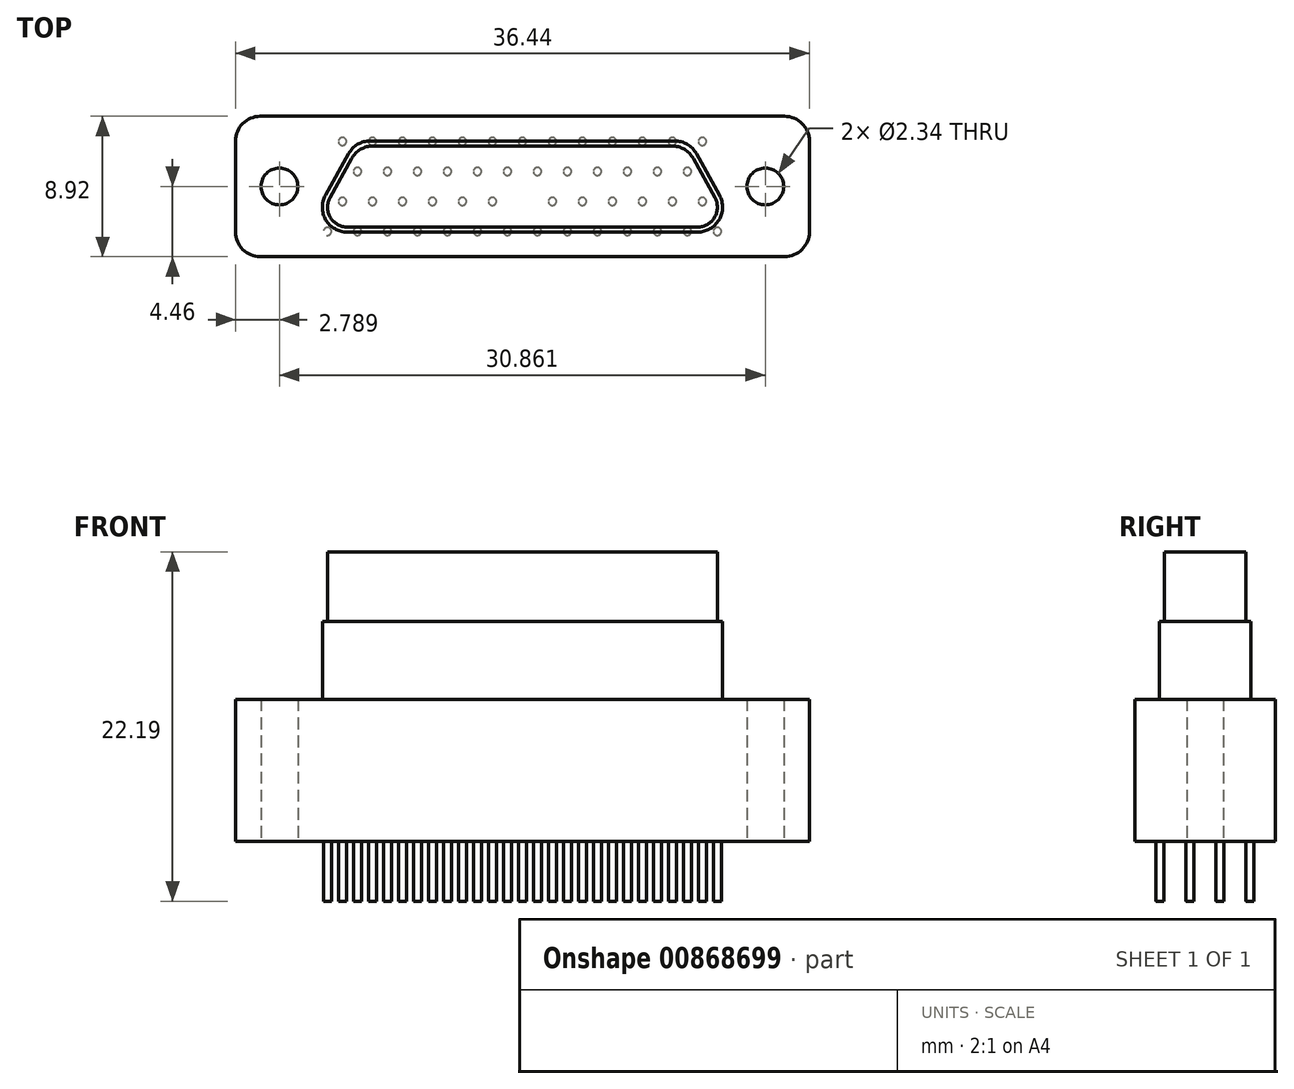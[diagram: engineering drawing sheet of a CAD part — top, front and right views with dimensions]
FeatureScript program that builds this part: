
annotation { "Feature Type Name" : "Feature", "Feature Type Description" : "" }
export const myFeature = defineFeature(function(context is Context, id is Id, definition is map)
    precondition{}
    {
        {
            var Q0;
            Q0=qCreatedBy(makeId("Top.planeOp"),FACE);
            var sketch = newSketch(context, id + "F0", { "sketchPlane" : qUnion([Q0])});
            skLineSegment(sketch, "E0.bottom", {"start": v(-16.65, 4.46) * mm, "end": v(16.65, 4.46) * mm});
            skLineSegment(sketch, "E0.top", {"start": v(-16.65, -4.46) * mm, "end": v(16.65, -4.46) * mm});
            skLineSegment(sketch, "E0.left", {"start": v(-18.22, 2.88) * mm, "end": v(-18.22, -2.88) * mm});
            skLineSegment(sketch, "E0.right", {"start": v(18.22, 2.88) * mm, "end": v(18.22, -2.88) * mm});
            skPoint(sketch, "E0.middle", {"position": v(0, 0) * mm});
            skCircle(sketch, "E1", {"center": v(-15.43, 0) * mm, "radius": 1.17 * mm});
            skCircle(sketch, "E2", {"center": v(15.43, 0) * mm, "radius": 1.17 * mm});
            skPoint(sketch, "E3.visualSharp", {"position": v(-18.22, -4.46) * mm});
            skArc(sketch, "E3.filletArc", {"start": v(-18.22, -2.88) * mm, "mid": v(-17.76, -4) * mm, "end": v(-16.65, -4.46) * mm});
            skPoint(sketch, "E4.visualSharp", {"position": v(-18.22, 4.46) * mm});
            skArc(sketch, "E4.filletArc", {"start": v(-16.65, 4.46) * mm, "mid": v(-17.76, 4) * mm, "end": v(-18.22, 2.88) * mm});
            skPoint(sketch, "E5.visualSharp", {"position": v(18.22, 4.46) * mm});
            skArc(sketch, "E5.filletArc", {"start": v(18.22, 2.88) * mm, "mid": v(17.76, 4) * mm, "end": v(16.65, 4.46) * mm});
            skPoint(sketch, "E6.visualSharp", {"position": v(18.22, -4.46) * mm});
            skArc(sketch, "E6.filletArc", {"start": v(16.65, -4.46) * mm, "mid": v(17.76, -4) * mm, "end": v(18.22, -2.88) * mm});
            skSolve(sketch);
        }
        {
            var Q0;
            Q0=makeQuery(id+"F0.imprint","IMPRINT",FACE,{"disambiguationData":[TD([[makeQuery(id+"F0.imprint","IMPRINT",EDGE,{"derivedFrom":sQuery(id+"F0.wireOp",EDGE,"E0.bottom")}),-1.0]])]});
            extrude(context, id + "F1", {"entities" : qUnion([Q0]), "endBound" : BoundingType.SYMMETRIC, "depth" : 9.02 * mm, "offsetDistance" : 25.4 * mm});
        }
        {
            var Q0;
            Q0=makeQuery(id+"F1.opExtrude","CAP_FACE",FACE,{"disambiguationData":[OSD([sQuery(id+"F0.wireOp",EDGE,"E0.bottom"),sQuery(id+"F0.wireOp",EDGE,"E0.top"),sQuery(id+"F0.wireOp",EDGE,"E0.left"),sQuery(id+"F0.wireOp",EDGE,"E0.right"),sQuery(id+"F0.wireOp",EDGE,"E1"),sQuery(id+"F0.wireOp",EDGE,"E2"),sQuery(id+"F0.wireOp",EDGE,"E3.filletArc"),sQuery(id+"F0.wireOp",EDGE,"E4.filletArc"),sQuery(id+"F0.wireOp",EDGE,"E5.filletArc"),sQuery(id+"F0.wireOp",EDGE,"E6.filletArc")])],"isStart":false});
            var sketch = newSketch(context, id + "F2", { "sketchPlane" : qUnion([Q0])});
            skPoint(sketch, "E7.middle", {"position": v(0, 0) * mm});
            skLineSegment(sketch, "E8.top", {"start": v(11.13, -2.9) * mm, "end": v(-11.13, -2.9) * mm});
            skLineSegment(sketch, "E9", {"start": v(-9.67, 2.9) * mm, "end": v(9.67, 2.9) * mm});
            skLineSegment(sketch, "E10", {"start": v(-12.5, -0.56) * mm, "end": v(-11.04, 2.08) * mm});
            skLineSegment(sketch, "E11", {"start": v(11.05, 2.08) * mm, "end": v(12.51, -0.56) * mm});
            skPoint(sketch, "E12.visualSharp", {"position": v(-10.6, 2.9) * mm});
            skArc(sketch, "E12.filletArc", {"start": v(-9.67, 2.9) * mm, "mid": v(-10.47, 2.68) * mm, "end": v(-11.04, 2.08) * mm});
            skPoint(sketch, "E13.visualSharp", {"position": v(-13.8, -2.9) * mm});
            skArc(sketch, "E13.filletArc", {"start": v(-12.5, -0.56) * mm, "mid": v(-12.49, -2.12) * mm, "end": v(-11.13, -2.9) * mm});
            skPoint(sketch, "E14.visualSharp", {"position": v(13.8, -2.9) * mm});
            skArc(sketch, "E14.filletArc", {"start": v(11.13, -2.9) * mm, "mid": v(12.49, -2.12) * mm, "end": v(12.51, -0.56) * mm});
            skPoint(sketch, "E15.visualSharp", {"position": v(10.6, 2.9) * mm});
            skArc(sketch, "E15.filletArc", {"start": v(11.05, 2.08) * mm, "mid": v(10.47, 2.68) * mm, "end": v(9.67, 2.9) * mm});
            skSolve(sketch);
        }
        {
            var Q0;
            Q0=qSketchRegion(id+"F2",true);
            extrude(context, id + "F3", {"entities" : qUnion([Q0]), "operationType" : NewBodyOperationType.ADD, "depth" : 4.95 * mm, "offsetDistance" : 25.4 * mm});
        }
        {
            var Q0;
            Q0=makeQuery(id+"F3.opExtrude","CAP_FACE",FACE,{"disambiguationData":[OSD([sQuery(id+"F2.wireOp",EDGE,"E8.top"),sQuery(id+"F2.wireOp",EDGE,"E9"),sQuery(id+"F2.wireOp",EDGE,"E10"),sQuery(id+"F2.wireOp",EDGE,"E11"),sQuery(id+"F2.wireOp",EDGE,"E12.filletArc"),sQuery(id+"F2.wireOp",EDGE,"E13.filletArc"),sQuery(id+"F2.wireOp",EDGE,"E14.filletArc"),sQuery(id+"F2.wireOp",EDGE,"E15.filletArc")])],"isStart":false});
            var sketch = newSketch(context, id + "F4", { "sketchPlane" : qUnion([Q0])});
            skLineSegment(sketch, "E16", {"start": v(-9.48, 2.58) * mm, "end": v(9.48, 2.58) * mm});
            skLineSegment(sketch, "E17", {"start": v(10.86, 1.77) * mm, "end": v(12.22, -0.7) * mm});
            skLineSegment(sketch, "E18", {"start": v(11.11, -2.58) * mm, "end": v(-11.1, -2.58) * mm});
            skLineSegment(sketch, "E19", {"start": v(-12.22, -0.7) * mm, "end": v(-10.86, 1.77) * mm});
            skPoint(sketch, "E20.visualSharp", {"position": v(-13.27, -2.58) * mm});
            skArc(sketch, "E20.filletArc", {"start": v(-12.22, -0.7) * mm, "mid": v(-12.2, -1.95) * mm, "end": v(-11.1, -2.58) * mm});
            skPoint(sketch, "E21.visualSharp", {"position": v(-10.4, 2.58) * mm});
            skArc(sketch, "E21.filletArc", {"start": v(-9.48, 2.58) * mm, "mid": v(-10.28, 2.36) * mm, "end": v(-10.86, 1.77) * mm});
            skPoint(sketch, "E22.visualSharp", {"position": v(10.4, 2.58) * mm});
            skArc(sketch, "E22.filletArc", {"start": v(10.86, 1.77) * mm, "mid": v(10.28, 2.36) * mm, "end": v(9.48, 2.58) * mm});
            skPoint(sketch, "E23.visualSharp", {"position": v(13.27, -2.58) * mm});
            skArc(sketch, "E23.filletArc", {"start": v(11.11, -2.58) * mm, "mid": v(12.2, -1.95) * mm, "end": v(12.22, -0.7) * mm});
            skSolve(sketch);
        }
        {
            var Q0;
            Q0=qSketchRegion(id+"F4",true);
            extrude(context, id + "F5", {"entities" : qUnion([Q0]), "operationType" : NewBodyOperationType.ADD, "depth" : 4.4 * mm, "offsetDistance" : 25.4 * mm});
        }
        {
            var Q0;
            Q0=makeQuery(id+"F1.opExtrude","CAP_FACE",FACE,{"disambiguationData":[OSD([sQuery(id+"F0.wireOp",EDGE,"E0.bottom"),sQuery(id+"F0.wireOp",EDGE,"E0.top"),sQuery(id+"F0.wireOp",EDGE,"E0.left"),sQuery(id+"F0.wireOp",EDGE,"E0.right"),sQuery(id+"F0.wireOp",EDGE,"E1"),sQuery(id+"F0.wireOp",EDGE,"E2"),sQuery(id+"F0.wireOp",EDGE,"E3.filletArc"),sQuery(id+"F0.wireOp",EDGE,"E4.filletArc"),sQuery(id+"F0.wireOp",EDGE,"E5.filletArc"),sQuery(id+"F0.wireOp",EDGE,"E6.filletArc")])],"isStart":true});
            var sketch = newSketch(context, id + "F6", { "sketchPlane" : qUnion([Q0])});
            skCircle(sketch, "E24", {"center": v(-12.38, 2.86) * mm, "radius": 0.25 * mm});
            skCircle(sketch, "E25.1.0.0", {"center": v(-10.48, 2.86) * mm, "radius": 0.25 * mm});
            skCircle(sketch, "E25.2.0.0", {"center": v(-8.57, 2.86) * mm, "radius": 0.25 * mm});
            skCircle(sketch, "E25.3.0.0", {"center": v(-6.67, 2.86) * mm, "radius": 0.25 * mm});
            skCircle(sketch, "E25.4.0.0", {"center": v(-4.76, 2.86) * mm, "radius": 0.25 * mm});
            skCircle(sketch, "E25.5.0.0", {"center": v(-2.86, 2.86) * mm, "radius": 0.25 * mm});
            skCircle(sketch, "E25.6.0.0", {"center": v(-0.95, 2.86) * mm, "radius": 0.25 * mm});
            skCircle(sketch, "E25.7.0.0", {"center": v(0.95, 2.86) * mm, "radius": 0.25 * mm});
            skCircle(sketch, "E25.8.0.0", {"center": v(2.86, 2.86) * mm, "radius": 0.25 * mm});
            skCircle(sketch, "E25.9.0.0", {"center": v(4.76, 2.86) * mm, "radius": 0.25 * mm});
            skCircle(sketch, "E25.10.0.0", {"center": v(6.67, 2.86) * mm, "radius": 0.25 * mm});
            skCircle(sketch, "E25.11.0.0", {"center": v(8.57, 2.86) * mm, "radius": 0.25 * mm});
            skCircle(sketch, "E25.12.0.0", {"center": v(10.48, 2.86) * mm, "radius": 0.25 * mm});
            skCircle(sketch, "E25.13.0.0", {"center": v(12.38, 2.86) * mm, "radius": 0.25 * mm});
            skLineSegment(sketch, "E25.direction1", {"start": v(-12.38, 2.86) * mm, "end": v(-10.48, 2.86) * mm, "construction": true});
            skCircle(sketch, "E26", {"center": v(-11.43, 0.95) * mm, "radius": 0.25 * mm});
            skCircle(sketch, "E27.1.0.0", {"center": v(-9.53, 0.95) * mm, "radius": 0.25 * mm});
            skCircle(sketch, "E27.2.0.0", {"center": v(-7.62, 0.95) * mm, "radius": 0.25 * mm});
            skCircle(sketch, "E27.3.0.0", {"center": v(-5.71, 0.95) * mm, "radius": 0.25 * mm});
            skCircle(sketch, "E27.4.0.0", {"center": v(-3.8, 0.95) * mm, "radius": 0.25 * mm});
            skCircle(sketch, "E27.5.0.0", {"center": v(-1.9, 0.95) * mm, "radius": 0.25 * mm});
            skLineSegment(sketch, "E27.direction1", {"start": v(-11.43, 0.95) * mm, "end": v(-9.53, 0.95) * mm, "construction": true});
            skCircle(sketch, "E28", {"center": v(-10.48, -0.95) * mm, "radius": 0.25 * mm});
            skCircle(sketch, "E29.1.0.0", {"center": v(-8.57, -0.95) * mm, "radius": 0.25 * mm});
            skCircle(sketch, "E29.2.0.0", {"center": v(-6.67, -0.95) * mm, "radius": 0.25 * mm});
            skCircle(sketch, "E29.3.0.0", {"center": v(-4.76, -0.95) * mm, "radius": 0.25 * mm});
            skCircle(sketch, "E29.4.0.0", {"center": v(-2.86, -0.95) * mm, "radius": 0.25 * mm});
            skCircle(sketch, "E29.5.0.0", {"center": v(-0.95, -0.95) * mm, "radius": 0.25 * mm});
            skLineSegment(sketch, "E29.direction1", {"start": v(-10.48, -0.95) * mm, "end": v(-8.57, -0.95) * mm, "construction": true});
            skLineSegment(sketch, "E30", {"start": v(0, 0.44) * mm, "end": v(0, -0.44) * mm});
            skLineSegment(sketch, "E31.MirrorCS", {"start": v(10.48, -0.95) * mm, "end": v(8.57, -0.95) * mm, "construction": true});
            skCircle(sketch, "E32.MirrorC", {"center": v(9.53, 0.95) * mm, "radius": 0.25 * mm});
            skCircle(sketch, "E33.MirrorC", {"center": v(7.62, 0.95) * mm, "radius": 0.25 * mm});
            skCircle(sketch, "E34.MirrorC", {"center": v(6.67, -0.95) * mm, "radius": 0.25 * mm});
            skCircle(sketch, "E35.MirrorC", {"center": v(11.43, 0.95) * mm, "radius": 0.25 * mm});
            skLineSegment(sketch, "E36.MirrorCS", {"start": v(11.43, 0.95) * mm, "end": v(9.53, 0.95) * mm, "construction": true});
            skCircle(sketch, "E37.MirrorC", {"center": v(4.76, -0.95) * mm, "radius": 0.25 * mm});
            skCircle(sketch, "E38.MirrorC", {"center": v(2.86, -0.95) * mm, "radius": 0.25 * mm});
            skCircle(sketch, "E39.MirrorC", {"center": v(5.71, 0.95) * mm, "radius": 0.25 * mm});
            skCircle(sketch, "E40.MirrorC", {"center": v(8.57, -0.95) * mm, "radius": 0.25 * mm});
            skCircle(sketch, "E41.MirrorC", {"center": v(1.9, 0.95) * mm, "radius": 0.25 * mm});
            skCircle(sketch, "E42.MirrorC", {"center": v(3.8, 0.95) * mm, "radius": 0.25 * mm});
            skCircle(sketch, "E43.MirrorC", {"center": v(10.48, -0.95) * mm, "radius": 0.25 * mm});
            skCircle(sketch, "E44.MirrorC", {"center": v(0.95, -0.95) * mm, "radius": 0.25 * mm});
            skCircle(sketch, "E45", {"center": v(-11.43, -2.86) * mm, "radius": 0.25 * mm});
            skCircle(sketch, "E46.1.0.0", {"center": v(-9.53, -2.86) * mm, "radius": 0.25 * mm});
            skCircle(sketch, "E46.2.0.0", {"center": v(-7.62, -2.86) * mm, "radius": 0.25 * mm});
            skCircle(sketch, "E46.3.0.0", {"center": v(-5.71, -2.86) * mm, "radius": 0.25 * mm});
            skCircle(sketch, "E46.4.0.0", {"center": v(-3.8, -2.86) * mm, "radius": 0.25 * mm});
            skCircle(sketch, "E46.5.0.0", {"center": v(-1.9, -2.86) * mm, "radius": 0.25 * mm});
            skCircle(sketch, "E46.6.0.0", {"center": v(0, -2.86) * mm, "radius": 0.25 * mm});
            skCircle(sketch, "E46.7.0.0", {"center": v(1.9, -2.86) * mm, "radius": 0.25 * mm});
            skCircle(sketch, "E46.8.0.0", {"center": v(3.81, -2.86) * mm, "radius": 0.25 * mm});
            skCircle(sketch, "E46.9.0.0", {"center": v(5.72, -2.86) * mm, "radius": 0.25 * mm});
            skCircle(sketch, "E46.10.0.0", {"center": v(7.62, -2.86) * mm, "radius": 0.25 * mm});
            skCircle(sketch, "E46.11.0.0", {"center": v(9.53, -2.86) * mm, "radius": 0.25 * mm});
            skCircle(sketch, "E46.12.0.0", {"center": v(11.43, -2.86) * mm, "radius": 0.25 * mm});
            skLineSegment(sketch, "E46.direction1", {"start": v(-11.43, -2.86) * mm, "end": v(-9.53, -2.86) * mm, "construction": true});
            skSolve(sketch);
        }
        {
            var Q0;
            Q0=qSketchRegion(id+"F6",true);
            extrude(context, id + "F7", {"entities" : qUnion([Q0]), "operationType" : NewBodyOperationType.ADD, "depth" : 3.8 * mm, "offsetDistance" : 25.4 * mm});
        }
    });
